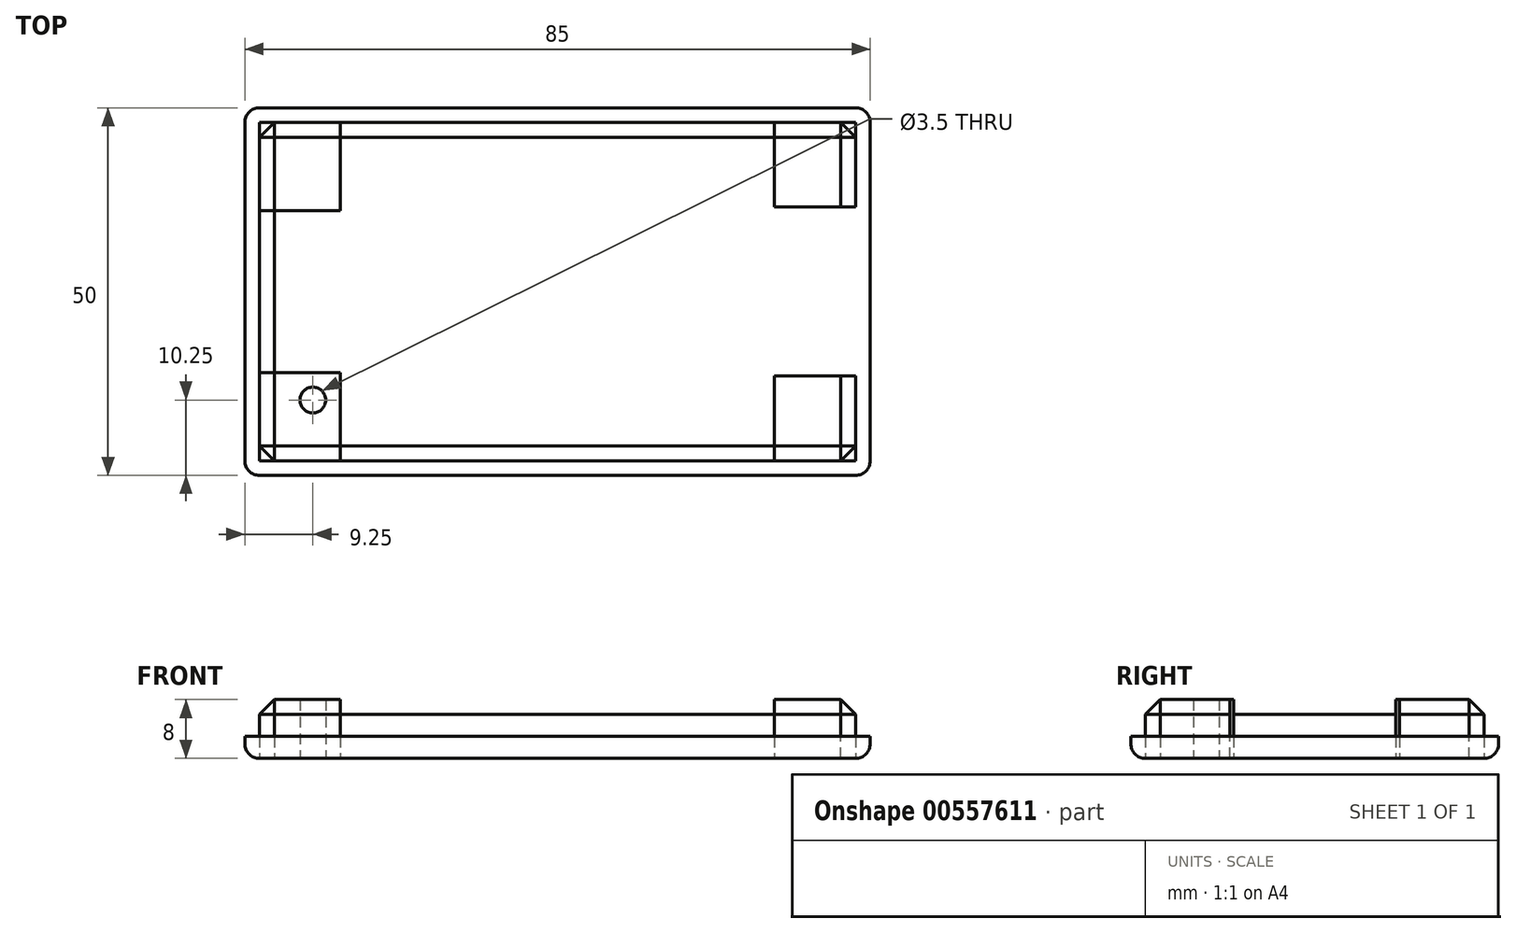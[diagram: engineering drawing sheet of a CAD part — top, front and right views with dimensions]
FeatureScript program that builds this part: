
annotation { "Feature Type Name" : "Feature", "Feature Type Description" : "" }
export const myFeature = defineFeature(function(context is Context, id is Id, definition is map)
    precondition{}
    {
        {
            var Q0;
            Q0=qCreatedBy(makeId("Top.planeOp"),FACE);
            var sketch = newSketch(context, id + "F0", { "sketchPlane" : qUnion([Q0])});
            skLineSegment(sketch, "E0.bottom", {"start": v(-42.5, 25) * mm, "end": v(42.5, 25) * mm});
            skLineSegment(sketch, "E0.top", {"start": v(-42.5, -25) * mm, "end": v(42.5, -25) * mm});
            skLineSegment(sketch, "E0.left", {"start": v(-42.5, 25) * mm, "end": v(-42.5, -25) * mm});
            skLineSegment(sketch, "E0.right", {"start": v(42.5, 25) * mm, "end": v(42.5, -25) * mm});
            skSolve(sketch);
        }
        {
            var Q0;
            Q0=qCreatedBy(makeId("Top.planeOp"),FACE);
            var sketch = newSketch(context, id + "F1", { "sketchPlane" : qUnion([Q0])});
            skCircle(sketch, "E1", {"center": v(34, 7.5) * mm, "radius": 3.04 * mm});
            skCircle(sketch, "E2", {"center": v(34, -7.5) * mm, "radius": 3.04 * mm});
            skCircle(sketch, "E3", {"center": v(34, 0) * mm, "radius": 3.04 * mm});
            skSolve(sketch);
        }
        {
            var Q0;
            Q0=qCreatedBy(makeId("Top.planeOp"),FACE);
            var sketch = newSketch(context, id + "F2", { "sketchPlane" : qUnion([Q0])});
            skCircle(sketch, "E4", {"center": v(-23, 0) * mm, "radius": 2.5 * mm});
            skCircle(sketch, "E5", {"center": v(15, 0) * mm, "radius": 2.5 * mm});
            skSolve(sketch);
        }
        {
            var Q0;
            Q0=qCreatedBy(makeId("Top.planeOp"),FACE);
            var sketch = newSketch(context, id + "F3", { "sketchPlane" : qUnion([Q0])});
            skCircle(sketch, "E6", {"center": v(-33.25, 14.75) * mm, "radius": 1.75 * mm});
            skCircle(sketch, "E7", {"center": v(-33.25, -14.75) * mm, "radius": 1.75 * mm});
            skCircle(sketch, "E8", {"center": v(33.25, 14.75) * mm, "radius": 1.75 * mm});
            skCircle(sketch, "E9", {"center": v(33.25, -14.75) * mm, "radius": 1.75 * mm});
            skSolve(sketch);
        }
        {
            var Q0;
            Q0=qCreatedBy(makeId("Top.planeOp"),FACE);
            var sketch = newSketch(context, id + "F4", { "sketchPlane" : qUnion([Q0])});
            skLineSegment(sketch, "E10.bottom", {"start": v(-40.5, 23) * mm, "end": v(40.5, 23) * mm});
            skLineSegment(sketch, "E10.top", {"start": v(-40.5, -23) * mm, "end": v(40.5, -23) * mm});
            skLineSegment(sketch, "E10.left", {"start": v(-40.5, 23) * mm, "end": v(-40.5, -23) * mm});
            skLineSegment(sketch, "E10.right", {"start": v(40.5, 23) * mm, "end": v(40.5, -23) * mm});
            skSolve(sketch);
        }
        {
            var Q0;
            Q0=qCreatedBy(makeId("Top.planeOp"),FACE);
            var sketch = newSketch(context, id + "F5", { "sketchPlane" : qUnion([Q0])});
            skLineSegment(sketch, "E11.bottom", {"start": v(-38.5, 21) * mm, "end": v(38.5, 21) * mm});
            skLineSegment(sketch, "E11.top", {"start": v(-38.5, -21) * mm, "end": v(38.5, -21) * mm});
            skLineSegment(sketch, "E11.left", {"start": v(-38.5, 21) * mm, "end": v(-38.5, -21) * mm});
            skLineSegment(sketch, "E11.right", {"start": v(38.5, 21) * mm, "end": v(38.5, -21) * mm});
            skSolve(sketch);
        }
        {
            var Q0;
            Q0=qCreatedBy(makeId("Top.planeOp"),FACE);
            var sketch = newSketch(context, id + "F6", { "sketchPlane" : qUnion([Q0])});
            skLineSegment(sketch, "E12.bottom", {"start": v(31.7, 11.5) * mm, "end": v(46.45, 11.5) * mm});
            skLineSegment(sketch, "E12.top", {"start": v(31.7, -11.5) * mm, "end": v(46.45, -11.5) * mm});
            skLineSegment(sketch, "E12.left", {"start": v(31.7, 11.5) * mm, "end": v(31.7, -11.5) * mm});
            skLineSegment(sketch, "E12.right", {"start": v(46.45, 11.5) * mm, "end": v(46.45, -11.5) * mm});
            skSolve(sketch);
        }
        {
            var Q0;
            Q0=qCreatedBy(makeId("Top.planeOp"),FACE);
            var sketch = newSketch(context, id + "F7", { "sketchPlane" : qUnion([Q0])});
            skLineSegment(sketch, "E13.bottom", {"start": v(-40.5, -11) * mm, "end": v(-29.5, -11) * mm});
            skLineSegment(sketch, "E13.top", {"start": v(-40.5, -23) * mm, "end": v(-29.5, -23) * mm});
            skLineSegment(sketch, "E13.left", {"start": v(-40.5, -11) * mm, "end": v(-40.5, -23) * mm});
            skLineSegment(sketch, "E13.right", {"start": v(-29.5, -11) * mm, "end": v(-29.5, -23) * mm});
            skLineSegment(sketch, "E14.bottom", {"start": v(29.5, -11.5) * mm, "end": v(40.5, -11.5) * mm});
            skLineSegment(sketch, "E14.top", {"start": v(29.5, -23) * mm, "end": v(40.5, -23) * mm});
            skLineSegment(sketch, "E14.left", {"start": v(29.5, -11.5) * mm, "end": v(29.5, -23) * mm});
            skLineSegment(sketch, "E14.right", {"start": v(40.5, -11.5) * mm, "end": v(40.5, -23) * mm});
            skLineSegment(sketch, "E15.bottom", {"start": v(29.5, 23) * mm, "end": v(40.5, 23) * mm});
            skLineSegment(sketch, "E15.top", {"start": v(29.5, 11.5) * mm, "end": v(40.5, 11.5) * mm});
            skLineSegment(sketch, "E15.left", {"start": v(29.5, 23) * mm, "end": v(29.5, 11.5) * mm});
            skLineSegment(sketch, "E15.right", {"start": v(40.5, 23) * mm, "end": v(40.5, 11.5) * mm});
            skLineSegment(sketch, "E16.bottom", {"start": v(-40.5, 23) * mm, "end": v(-29.5, 23) * mm});
            skLineSegment(sketch, "E16.top", {"start": v(-40.5, 11) * mm, "end": v(-29.5, 11) * mm});
            skLineSegment(sketch, "E16.left", {"start": v(-40.5, 23) * mm, "end": v(-40.5, 11) * mm});
            skLineSegment(sketch, "E16.right", {"start": v(-29.5, 23) * mm, "end": v(-29.5, 11) * mm});
            skSolve(sketch);
        }
        {
            var Q0;
            Q0=qSketchRegion(id+"F0",true);
            extrude(context, id + "F8", {"entities" : qUnion([Q0]), "depth" : 3 * mm, "offsetDistance" : 25 * mm});
        }
        {
            var Q0;
            Q0=makeQuery(id+"F8.opExtrude","CAP_EDGE",EDGE,{"disambiguationData":[OSD([sQuery(id+"F0.wireOp",EDGE,"E0.top")])],"isStart":true});
            var Q1;
            Q1=makeQuery(id+"F8.opExtrude","CAP_EDGE",EDGE,{"disambiguationData":[OSD([sQuery(id+"F0.wireOp",EDGE,"E0.right")])],"isStart":true});
            var Q2;
            Q2=makeQuery(id+"F8.opExtrude","CAP_EDGE",EDGE,{"disambiguationData":[OSD([sQuery(id+"F0.wireOp",EDGE,"E0.bottom")])],"isStart":true});
            var Q3;
            Q3=makeQuery(id+"F8.opExtrude","CAP_EDGE",EDGE,{"disambiguationData":[OSD([sQuery(id+"F0.wireOp",EDGE,"E0.left")])],"isStart":true});
            var Q4;
            Q4=makeQuery(id+"F8.opExtrude","SWEPT_EDGE",EDGE,{"disambiguationData":[OSD([sQuery(id+"F0.wireOp",EDGE,"E0.bottom"),sQuery(id+"F0.wireOp",EDGE,"E0.left")])]});
            var Q5;
            Q5=makeQuery(id+"F8.opExtrude","SWEPT_EDGE",EDGE,{"disambiguationData":[OSD([sQuery(id+"F0.wireOp",EDGE,"E0.top"),sQuery(id+"F0.wireOp",EDGE,"E0.left")])]});
            var Q6;
            Q6=makeQuery(id+"F8.opExtrude","SWEPT_EDGE",EDGE,{"disambiguationData":[OSD([sQuery(id+"F0.wireOp",EDGE,"E0.top"),sQuery(id+"F0.wireOp",EDGE,"E0.right")])]});
            var Q7;
            Q7=makeQuery(id+"F8.opExtrude","SWEPT_EDGE",EDGE,{"disambiguationData":[OSD([sQuery(id+"F0.wireOp",EDGE,"E0.bottom"),sQuery(id+"F0.wireOp",EDGE,"E0.right")])]});
            fillet(context, id + "F9", {"entities" : qUnion([Q0, Q1, Q2, Q3, Q4, Q5, Q6, Q7]), "radius" : 2 * mm, "tangentPropagation" : true, "allowEdgeOverflow" : false});
        }
        {
            var Q0;
            Q0=qSketchRegion(id+"F1",true);
            extrude(context, id + "F10", {"entities" : qUnion([Q0]), "depth" : 5 * mm, "offsetDistance" : 25 * mm});
        }
        {
            var Q0;
            Q0=qSketchRegion(id+"F2",true);
            extrude(context, id + "F11", {"entities" : qUnion([Q0]), "depth" : 5 * mm, "offsetDistance" : 25 * mm});
        }
        {
            var Q0;
            Q0=qSketchRegion(id+"F4",true);
            extrude(context, id + "F12", {"entities" : qUnion([Q0]), "depth" : 6 * mm, "offsetDistance" : 25 * mm});
        }
        {
            var Q0;
            Q0=qSketchRegion(id+"F5",true);
            extrude(context, id + "F13", {"entities" : qUnion([Q0]), "depth" : 6 * mm, "offsetDistance" : 25 * mm});
        }
        {
            var Q0;
            Q0=qSketchRegion(id+"F6",true);
            extrude(context, id + "F14", {"entities" : qUnion([Q0]), "depth" : 6 * mm, "offsetDistance" : 25 * mm});
        }
        {
            var Q0;
            Q0=makeQuery(id+"F7.imprint","IMPRINT",FACE,{"disambiguationData":[TD([[makeQuery(id+"F7.imprint","IMPRINT",EDGE,{"derivedFrom":sQuery(id+"F7.wireOp",EDGE,"E13.bottom")}),-1.0]])]});
            var Q1;
            Q1=makeQuery(id+"F7.imprint","IMPRINT",FACE,{"disambiguationData":[TD([[makeQuery(id+"F7.imprint","IMPRINT",EDGE,{"derivedFrom":sQuery(id+"F7.wireOp",EDGE,"E16.bottom")}),-1.0]])]});
            var Q2;
            Q2=makeQuery(id+"F7.imprint","IMPRINT",FACE,{"disambiguationData":[TD([[makeQuery(id+"F7.imprint","IMPRINT",EDGE,{"derivedFrom":sQuery(id+"F7.wireOp",EDGE,"E15.bottom")}),-1.0]])]});
            var Q3;
            Q3=makeQuery(id+"F7.imprint","IMPRINT",FACE,{"disambiguationData":[TD([[makeQuery(id+"F7.imprint","IMPRINT",EDGE,{"derivedFrom":sQuery(id+"F7.wireOp",EDGE,"E14.bottom")}),-1.0]])]});
            extrude(context, id + "F15", {"entities" : qUnion([Q0, Q1, Q2, Q3]), "depth" : 8 * mm, "offsetDistance" : 25 * mm});
        }
        {
            var Q0;
            Q0=makeQuery(id+"F3.imprint","IMPRINT",FACE,{"disambiguationData":[TD([[makeQuery(id+"F3.imprint","IMPRINT",EDGE,{"derivedFrom":sQuery(id+"F3.wireOp",EDGE,"E7")}),1.0]])]});
            var Q1;
            Q1=makeQuery(id+"F3.imprint","IMPRINT",FACE,{"disambiguationData":[TD([[makeQuery(id+"F3.imprint","IMPRINT",EDGE,{"derivedFrom":sQuery(id+"F3.wireOp",EDGE,"E9")}),1.0]])]});
            var Q2;
            Q2=makeQuery(id+"F3.imprint","IMPRINT",FACE,{"disambiguationData":[TD([[makeQuery(id+"F3.imprint","IMPRINT",EDGE,{"derivedFrom":sQuery(id+"F3.wireOp",EDGE,"E8")}),1.0]])]});
            var Q3;
            Q3=makeQuery(id+"F3.imprint","IMPRINT",FACE,{"disambiguationData":[TD([[makeQuery(id+"F3.imprint","IMPRINT",EDGE,{"derivedFrom":sQuery(id+"F3.wireOp",EDGE,"E6")}),1.0]])]});
            extrude(context, id + "F16", {"entities" : qUnion([Q0, Q1, Q2, Q3]), "depth" : 8 * mm, "offsetDistance" : 25 * mm});
        }
        {
            var Q0;
            Q0=makeQuery(id+"F13.opExtrude","SWEPT_BODY",BODY,{"disambiguationData":[OSD([sQuery(id+"F5.wireOp",EDGE,"E11.bottom"),sQuery(id+"F5.wireOp",EDGE,"E11.top"),sQuery(id+"F5.wireOp",EDGE,"E11.left"),sQuery(id+"F5.wireOp",EDGE,"E11.right")])]});
            var Q1;
            Q1=makeQuery(id+"F12.opExtrude","SWEPT_BODY",BODY,{"disambiguationData":[OSD([sQuery(id+"F4.wireOp",EDGE,"E10.bottom"),sQuery(id+"F4.wireOp",EDGE,"E10.top"),sQuery(id+"F4.wireOp",EDGE,"E10.left"),sQuery(id+"F4.wireOp",EDGE,"E10.right")])]});
            booleanBodies(context, id + "F17", {"operationType" : BooleanOperationType.SUBTRACTION, "tools" : qUnion([Q0]), "targets" : qUnion([Q1])});
        }
        {
            var Q0;
            Q0=makeQuery(id+"F14.opExtrude","SWEPT_BODY",BODY,{"disambiguationData":[OSD([sQuery(id+"F6.wireOp",EDGE,"E12.bottom"),sQuery(id+"F6.wireOp",EDGE,"E12.top"),sQuery(id+"F6.wireOp",EDGE,"E12.left"),sQuery(id+"F6.wireOp",EDGE,"E12.right")])]});
            var Q1;
            Q1=makeQuery(id+"F12.opExtrude","SWEPT_BODY",BODY,{"disambiguationData":[OSD([sQuery(id+"F4.wireOp",EDGE,"E10.bottom"),sQuery(id+"F4.wireOp",EDGE,"E10.top"),sQuery(id+"F4.wireOp",EDGE,"E10.left"),sQuery(id+"F4.wireOp",EDGE,"E10.right")])]});
            booleanBodies(context, id + "F18", {"operationType" : BooleanOperationType.SUBTRACTION, "tools" : qUnion([Q0]), "targets" : qUnion([Q1])});
        }
        {
            var Q0;
            Q0=makeQuery(id+"F10.opExtrude","SWEPT_BODY",BODY,{"disambiguationData":[OSD([sQuery(id+"F1.wireOp",EDGE,"E1")])]});
            var Q1;
            Q1=makeQuery(id+"F10.opExtrude","SWEPT_BODY",BODY,{"disambiguationData":[OSD([sQuery(id+"F1.wireOp",EDGE,"E3")])]});
            var Q2;
            Q2=makeQuery(id+"F10.opExtrude","SWEPT_BODY",BODY,{"disambiguationData":[OSD([sQuery(id+"F1.wireOp",EDGE,"E2")])]});
            var Q3;
            Q3=makeQuery(id+"F15.opExtrude","SWEPT_BODY",BODY,{"disambiguationData":[OSD([sQuery(id+"F7.wireOp",EDGE,"E13.bottom"),sQuery(id+"F7.wireOp",EDGE,"E13.top"),sQuery(id+"F7.wireOp",EDGE,"E13.left"),sQuery(id+"F7.wireOp",EDGE,"E13.right")])]});
            booleanBodies(context, id + "F19", {"operationType" : BooleanOperationType.SUBTRACTION, "tools" : qUnion([Q0, Q1, Q2]), "targets" : qUnion([Q3])});
        }
        {
            var Q0;
            Q0=makeQuery(id+"F11.opExtrude","SWEPT_BODY",BODY,{"disambiguationData":[OSD([sQuery(id+"F2.wireOp",EDGE,"E4")])]});
            var Q1;
            Q1=makeQuery(id+"F11.opExtrude","SWEPT_BODY",BODY,{"disambiguationData":[OSD([sQuery(id+"F2.wireOp",EDGE,"E5")])]});
            var Q2;
            Q2=makeQuery(id+"F15.opExtrude","SWEPT_BODY",BODY,{"disambiguationData":[OSD([sQuery(id+"F7.wireOp",EDGE,"E13.bottom"),sQuery(id+"F7.wireOp",EDGE,"E13.top"),sQuery(id+"F7.wireOp",EDGE,"E13.left"),sQuery(id+"F7.wireOp",EDGE,"E13.right")])]});
            booleanBodies(context, id + "F20", {"operationType" : BooleanOperationType.SUBTRACTION, "tools" : qUnion([Q0, Q1]), "targets" : qUnion([Q2])});
        }
        {
            var Q0;
            Q0=makeQuery(id+"F16.opExtrude","SWEPT_BODY",BODY,{"disambiguationData":[OSD([sQuery(id+"F3.wireOp",EDGE,"E7")])]});
            var Q1;
            Q1=makeQuery(id+"F16.opExtrude","SWEPT_BODY",BODY,{"disambiguationData":[OSD([sQuery(id+"F3.wireOp",EDGE,"E6")])]});
            var Q2;
            Q2=makeQuery(id+"F16.opExtrude","SWEPT_BODY",BODY,{"disambiguationData":[OSD([sQuery(id+"F3.wireOp",EDGE,"E8")])]});
            var Q3;
            Q3=makeQuery(id+"F16.opExtrude","SWEPT_BODY",BODY,{"disambiguationData":[OSD([sQuery(id+"F3.wireOp",EDGE,"E9")])]});
            var Q4;
            Q4=makeQuery(id+"F15.opExtrude","SWEPT_BODY",BODY,{"disambiguationData":[OSD([sQuery(id+"F7.wireOp",EDGE,"E13.bottom"),sQuery(id+"F7.wireOp",EDGE,"E13.top"),sQuery(id+"F7.wireOp",EDGE,"E13.left"),sQuery(id+"F7.wireOp",EDGE,"E13.right")])]});
            booleanBodies(context, id + "F21", {"operationType" : BooleanOperationType.SUBTRACTION, "tools" : qUnion([Q0, Q1, Q2, Q3]), "targets" : qUnion([Q4])});
        }
        {
            var Q0;
            Q0=qCreatedBy(makeId("Top.planeOp"),FACE);
            cPlane(context, id + "F22", {"entities" : qUnion([Q0]), "cplaneType" : CPlaneType.OFFSET, "offset" : 2 * mm, "width" : 150 * mm, "height" : 150 * mm});
        }
        {
            var Q0;
            Q0=qCreatedBy(id+"F22.planeOp",FACE);
            var sketch = newSketch(context, id + "F23", { "sketchPlane" : qUnion([Q0])});
            skLineSegment(sketch, "E17.bottom", {"start": v(29.5, 11.5) * mm, "end": v(39, 11.5) * mm});
            skLineSegment(sketch, "E17.top", {"start": v(29.5, -11.5) * mm, "end": v(39, -11.5) * mm});
            skLineSegment(sketch, "E17.left", {"start": v(29.5, 11.5) * mm, "end": v(29.5, -11.5) * mm});
            skLineSegment(sketch, "E17.right", {"start": v(39, 11.5) * mm, "end": v(39, -11.5) * mm});
            skSolve(sketch);
        }
        {
            var Q0;
            Q0=qSketchRegion(id+"F23",true);
            extrude(context, id + "F24", {"entities" : qUnion([Q0]), "depth" : 2 * mm, "offsetDistance" : 25 * mm});
        }
        {
            var Q0;
            Q0=makeQuery(id+"F24.opExtrude","SWEPT_BODY",BODY,{"disambiguationData":[OSD([sQuery(id+"F23.wireOp",EDGE,"E17.bottom"),sQuery(id+"F23.wireOp",EDGE,"E17.top"),sQuery(id+"F23.wireOp",EDGE,"E17.left"),sQuery(id+"F23.wireOp",EDGE,"E17.right")])]});
            var Q1;
            Q1=makeQuery(id+"F15.opExtrude","SWEPT_BODY",BODY,{"disambiguationData":[OSD([sQuery(id+"F7.wireOp",EDGE,"E13.bottom"),sQuery(id+"F7.wireOp",EDGE,"E13.top"),sQuery(id+"F7.wireOp",EDGE,"E13.left"),sQuery(id+"F7.wireOp",EDGE,"E13.right")])]});
            booleanBodies(context, id + "F25", {"operationType" : BooleanOperationType.SUBTRACTION, "tools" : qUnion([Q0]), "targets" : qUnion([Q1])});
        }
        {
            var Q0;
            Q0=makeQuery(id+"F15.opExtrude","SWEPT_EDGE",EDGE,{"disambiguationData":[OSD([sQuery(id+"F7.wireOp",EDGE,"E14.top"),sQuery(id+"F7.wireOp",EDGE,"E14.right")])]});
            var Q1;
            Q1=makeQuery(id+"F15.opExtrude","CAP_EDGE",EDGE,{"disambiguationData":[OSD([sQuery(id+"F7.wireOp",EDGE,"E14.top")])],"isStart":false});
            var Q2;
            Q2=makeQuery(id+"F15.opExtrude","CAP_EDGE",EDGE,{"disambiguationData":[OSD([sQuery(id+"F7.wireOp",EDGE,"E14.right")])],"isStart":false});
            var Q3;
            Q3=makeQuery(id+"F15.opExtrude","CAP_EDGE",EDGE,{"disambiguationData":[OSD([sQuery(id+"F7.wireOp",EDGE,"E13.top")])],"isStart":false});
            var Q4;
            Q4=makeQuery(id+"F15.opExtrude","SWEPT_EDGE",EDGE,{"disambiguationData":[OSD([sQuery(id+"F7.wireOp",EDGE,"E13.top"),sQuery(id+"F7.wireOp",EDGE,"E13.left")])]});
            var Q5;
            Q5=makeQuery(id+"F15.opExtrude","CAP_EDGE",EDGE,{"disambiguationData":[OSD([sQuery(id+"F7.wireOp",EDGE,"E13.left")])],"isStart":false});
            var Q6;
            Q6=makeQuery(id+"F15.opExtrude","CAP_EDGE",EDGE,{"disambiguationData":[OSD([sQuery(id+"F7.wireOp",EDGE,"E16.left")])],"isStart":false});
            var Q7;
            Q7=makeQuery(id+"F15.opExtrude","CAP_EDGE",EDGE,{"disambiguationData":[OSD([sQuery(id+"F7.wireOp",EDGE,"E16.bottom")])],"isStart":false});
            var Q8;
            Q8=makeQuery(id+"F15.opExtrude","SWEPT_EDGE",EDGE,{"disambiguationData":[OSD([sQuery(id+"F7.wireOp",EDGE,"E16.bottom"),sQuery(id+"F7.wireOp",EDGE,"E16.left")])]});
            var Q9;
            Q9=makeQuery(id+"F15.opExtrude","CAP_EDGE",EDGE,{"disambiguationData":[OSD([sQuery(id+"F7.wireOp",EDGE,"E15.bottom")])],"isStart":false});
            var Q10;
            Q10=makeQuery(id+"F15.opExtrude","SWEPT_EDGE",EDGE,{"disambiguationData":[OSD([sQuery(id+"F7.wireOp",EDGE,"E15.bottom"),sQuery(id+"F7.wireOp",EDGE,"E15.right")])]});
            var Q11;
            Q11=makeQuery(id+"F15.opExtrude","CAP_EDGE",EDGE,{"disambiguationData":[OSD([sQuery(id+"F7.wireOp",EDGE,"E15.right")])],"isStart":false});
            chamfer(context, id + "F26", {"entities" : qUnion([Q0, Q1, Q2, Q3, Q4, Q5, Q6, Q7, Q8, Q9, Q10, Q11]), "width" : 2 * mm, "tangentPropagation" : true});
        }
    });
